# Revit family: Sanitary_Showers_AXOR_48489USA-AXOR-One-Overhead-shower-75-1je_new
name_source: partatom
category: Plumbing Fixtures
revit_build: Autodesk Revit 2018 (Build: 20170223_1515(x64)
units: mm (PartAtom-declared; Revit-internal decimal feet)

## family parameters
Always vertical = No
Cut with Voids When Loaded = No
OmniClass Number = 23.31.17.00
OmniClass Title = Showers
Part Type = Normal
Room Calculation Point = No
Round Connector Dimension = Use Diameter
Shared = No
Work Plane-Based = Yes

## types (3) — shared parameters
Always visible = Yes
BIMobject category = Showers
Default Elevation = 1219.2 mm  [stored 4 ft]
Description = AXOR One Overhead shower 75 1jet 1.5 GPM with shower arm
Design country = Germany
EAN code = 4059625329443
Edition number = 1
IFC Classification = Sanitary Terminal
Installation instructions = https://www.axor-design.com
Manufacturer = AXOR
Manufacturer country = Germany
Manufacturer name = AXOR
Material 1 = AXOR - Plastic - Graphite
Material main = Chrome
Model = 48489USA
OmniClass Code = 23-31 17 00
OmniClass Description = Showers
Product Guid = 36e25583-70b8-4d48-a9b5-382d96541ba1
Product SKU = 48489USA
Product data url = https://bimobject.com
Product family = AXOR One
Product group = Overhead showers
Product name = 48489USA AXOR One Overhead shower 75 1jet 1.5 GPM with shower arm
Product url = https://www.axor-design.com
QR code = https://bimobject.com
URL = https://www.axor-design.com
Water Inlet = 13 mm
Water Inlet Description = Water Inlet 12.7mm
Weight Net (Kg) = 580

## per-type parameters (varying)
| type | Material 2 |
| 341 Brushed Black Chrome | AXOR - Metal - 341 Brushed Black Chrome |
| 821 Brushed Nickel | AXOR - Metal - 821 Brushed Nickel |
| 251 Brushed Gold Optic | AXOR - Metal - 251 Brushed Gold Optic |

note: [stored X ft] marks values corroborated as IEEE doubles in the binary element streams (Revit-internal decimal feet)

## geometry (parser evidence)
native form markers: Sweep x1
no freeform markers — native parametric forms only
